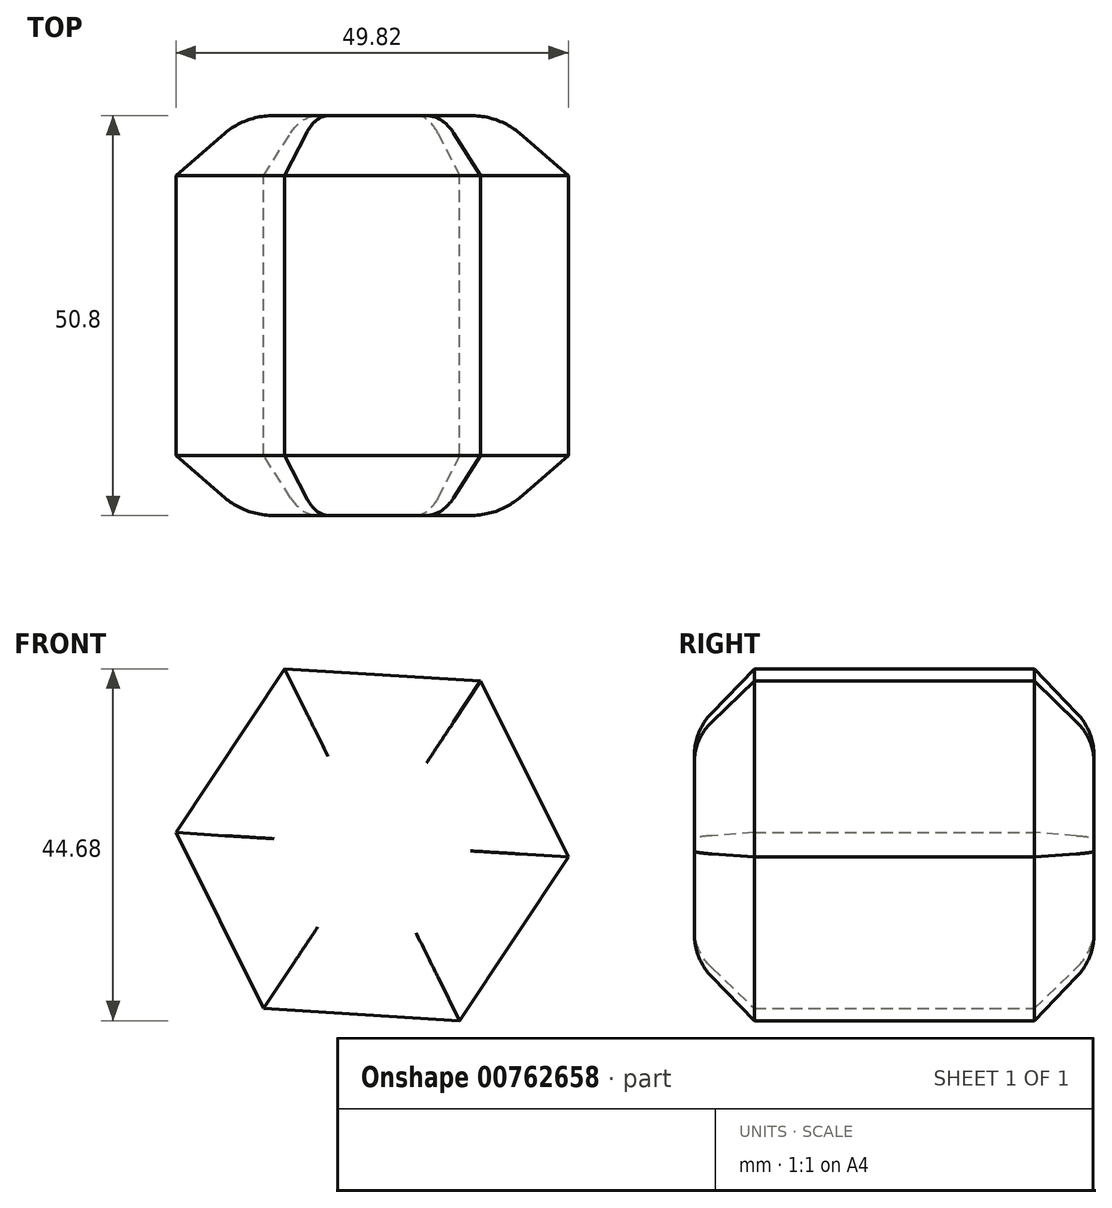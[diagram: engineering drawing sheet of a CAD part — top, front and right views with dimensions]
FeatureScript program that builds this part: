
annotation { "Feature Type Name" : "Feature", "Feature Type Description" : "" }
export const myFeature = defineFeature(function(context is Context, id is Id, definition is map)
    precondition{}
    {
        {
            var Q0;
            Q0=qCreatedBy(makeId("Front.planeOp"),FACE);
            var sketch = newSketch(context, id + "F0", { "sketchPlane" : qUnion([Q0])});
            skCircle(sketch, "E0.cCircle", {"center": v(-31.19, 45.22) * mm, "radius": 21.61 * mm, "construction": true});
            skLineSegment(sketch, "E0.0", {"start": v(-6.28, 43.67) * mm, "end": v(-20.07, 22.88) * mm});
            skLineSegment(sketch, "E0.1", {"start": v(-20.07, 22.88) * mm, "end": v(-44.98, 24.42) * mm});
            skLineSegment(sketch, "E0.2", {"start": v(-44.98, 24.42) * mm, "end": v(-56.1, 46.76) * mm});
            skLineSegment(sketch, "E0.3", {"start": v(-56.1, 46.76) * mm, "end": v(-42.3, 67.56) * mm});
            skLineSegment(sketch, "E0.4", {"start": v(-42.3, 67.56) * mm, "end": v(-17.4, 66.02) * mm});
            skLineSegment(sketch, "E0.5", {"start": v(-17.4, 66.02) * mm, "end": v(-6.28, 43.67) * mm});
            skPoint(sketch, "E0.0.midPoint", {"position": v(-13.18, 33.27) * mm});
            skSolve(sketch);
        }
        {
            var Q0;
            Q0=makeQuery(id+"F0.imprint","IMPRINT",FACE,{"disambiguationData":[TD([[makeQuery(id+"F0.imprint","IMPRINT",EDGE,{"derivedFrom":sQuery(id+"F0.wireOp",EDGE,"E0.0")}),-1.0]])]});
            extrude(context, id + "F1", {"entities" : qUnion([Q0]), "depth" : 25.4 * mm, "offsetDistance" : 25.4 * mm, "hasSecondDirection" : true, "secondDirectionOppositeDirection" : true, "secondDirectionDepth" : 25.4 * mm});
        }
        {
            var Q0;
            Q0=makeQuery(id+"F1.opExtrude","CAP_EDGE",EDGE,{"disambiguationData":[OSD([sQuery(id+"F0.wireOp",EDGE,"E0.4")])],"isStart":false});
            var Q1;
            Q1=makeQuery(id+"F1.opExtrude","CAP_EDGE",EDGE,{"disambiguationData":[OSD([sQuery(id+"F0.wireOp",EDGE,"E0.5")])],"isStart":false});
            var Q2;
            Q2=makeQuery(id+"F1.opExtrude","CAP_FACE",FACE,{"disambiguationData":[OSD([sQuery(id+"F0.wireOp",EDGE,"E0.0"),sQuery(id+"F0.wireOp",EDGE,"E0.1"),sQuery(id+"F0.wireOp",EDGE,"E0.2"),sQuery(id+"F0.wireOp",EDGE,"E0.3"),sQuery(id+"F0.wireOp",EDGE,"E0.4"),sQuery(id+"F0.wireOp",EDGE,"E0.5")])],"isStart":false});
            var Q3;
            Q3=makeQuery(id+"F1.opExtrude","CAP_FACE",FACE,{"disambiguationData":[OSD([sQuery(id+"F0.wireOp",EDGE,"E0.0"),sQuery(id+"F0.wireOp",EDGE,"E0.1"),sQuery(id+"F0.wireOp",EDGE,"E0.2"),sQuery(id+"F0.wireOp",EDGE,"E0.3"),sQuery(id+"F0.wireOp",EDGE,"E0.4"),sQuery(id+"F0.wireOp",EDGE,"E0.5")])],"isStart":true});
            chamfer(context, id + "F2", {"entities" : qUnion([Q0, Q1, Q2, Q3]), "width" : 7.62 * mm, "tangentPropagation" : true});
        }
        {
            var Q0;
            Q0=makeQuery(id+"F1.opExtrude","CAP_FACE",FACE,{"disambiguationData":[OSD([sQuery(id+"F0.wireOp",EDGE,"E0.0"),sQuery(id+"F0.wireOp",EDGE,"E0.1"),sQuery(id+"F0.wireOp",EDGE,"E0.2"),sQuery(id+"F0.wireOp",EDGE,"E0.3"),sQuery(id+"F0.wireOp",EDGE,"E0.4"),sQuery(id+"F0.wireOp",EDGE,"E0.5")])],"isStart":false});
            fillet(context, id + "F3", {"entities" : qUnion([Q0]), "radius" : 7.62 * mm, "tangentPropagation" : true, "allowEdgeOverflow" : false});
        }
        {
            var Q0;
            Q0=makeQuery(id+"F1.opExtrude","CAP_FACE",FACE,{"disambiguationData":[OSD([sQuery(id+"F0.wireOp",EDGE,"E0.0"),sQuery(id+"F0.wireOp",EDGE,"E0.1"),sQuery(id+"F0.wireOp",EDGE,"E0.2"),sQuery(id+"F0.wireOp",EDGE,"E0.3"),sQuery(id+"F0.wireOp",EDGE,"E0.4"),sQuery(id+"F0.wireOp",EDGE,"E0.5")])],"isStart":true});
            fillet(context, id + "F4", {"entities" : qUnion([Q0]), "radius" : 7.62 * mm, "tangentPropagation" : true, "allowEdgeOverflow" : false});
        }
    });
